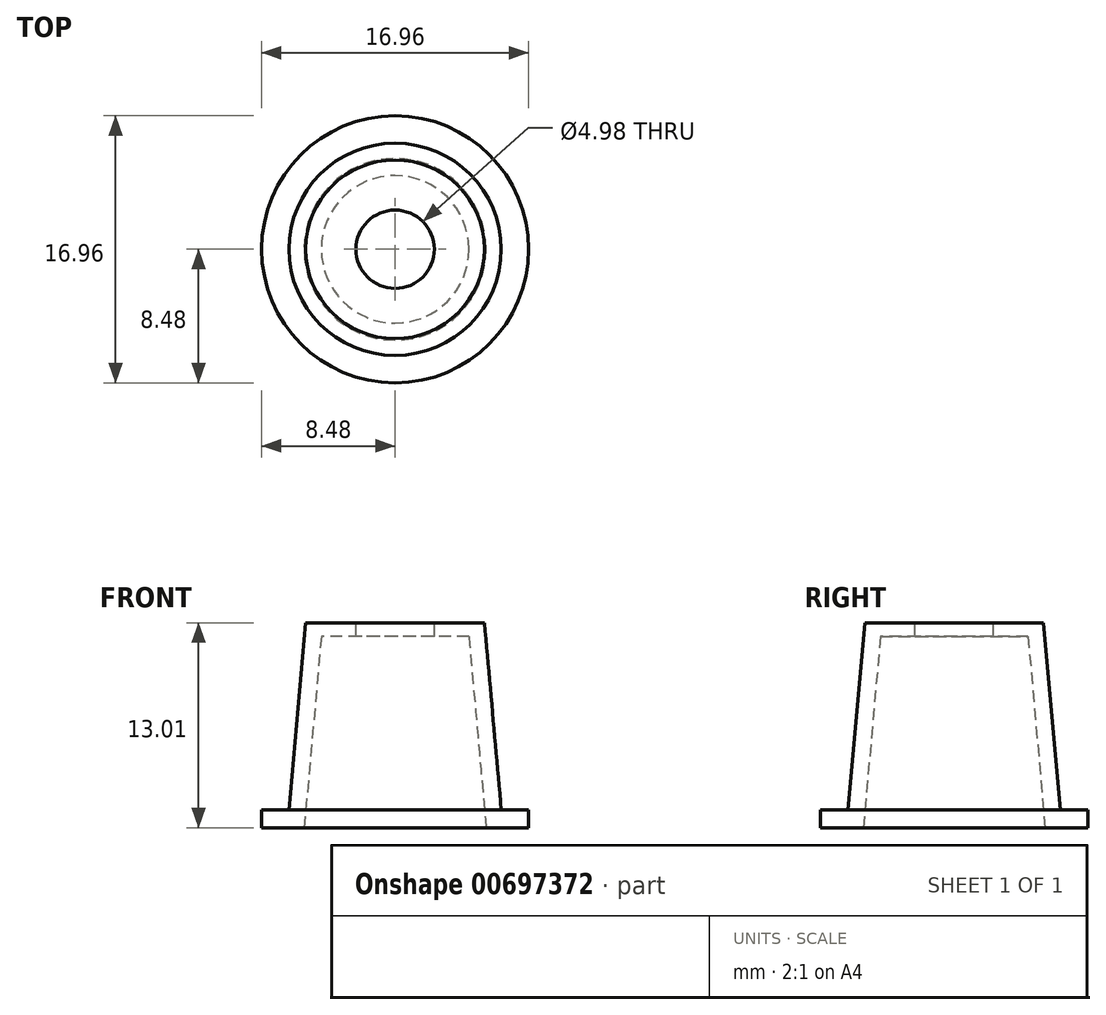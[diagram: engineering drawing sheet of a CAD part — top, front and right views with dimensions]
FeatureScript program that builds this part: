
annotation { "Feature Type Name" : "Feature", "Feature Type Description" : "" }
export const myFeature = defineFeature(function(context is Context, id is Id, definition is map)
    precondition{}
    {
        {
            var Q0;
            Q0=qCreatedBy(makeId("Front.planeOp"),FACE);
            var sketch = newSketch(context, id + "F0", { "sketchPlane" : qUnion([Q0])});
            skLineSegment(sketch, "E0", {"start": v(-8.48, 0) * mm, "end": v(-8.48, 1.13) * mm});
            skLineSegment(sketch, "E1", {"start": v(-8.48, 1.13) * mm, "end": v(-6.74, 1.13) * mm});
            skLineSegment(sketch, "E2", {"start": v(-5.68, 13.01) * mm, "end": v(-6.74, 1.13) * mm});
            skLineSegment(sketch, "E3", {"start": v(-5.68, 13.01) * mm, "end": v(-2.49, 13.01) * mm});
            skLineSegment(sketch, "E4", {"start": v(-2.49, 13.01) * mm, "end": v(-2.49, 12.16) * mm});
            skLineSegment(sketch, "E5", {"start": v(-2.49, 12.16) * mm, "end": v(-4.69, 12.16) * mm});
            skLineSegment(sketch, "E6", {"start": v(-4.69, 12.16) * mm, "end": v(-5.77, 0) * mm});
            skLineSegment(sketch, "E7", {"start": v(-8.48, 0) * mm, "end": v(-5.77, 0) * mm});
            skLineSegment(sketch, "E8", {"start": v(0, 15.54) * mm, "end": v(0, -0.82) * mm, "construction": true});
            skSolve(sketch);
        }
        {
            var Q0;
            Q0=makeQuery(id+"F0.imprint","IMPRINT",FACE,{"disambiguationData":[TD([[makeQuery(id+"F0.imprint","IMPRINT",EDGE,{"derivedFrom":sQuery(id+"F0.wireOp",EDGE,"E0")}),-1.0]])]});
            var Q1;
            Q1=sQuery(id+"F0.wireOp",EDGE,"E8");
            revolve(context, id + "F1", {"surfaceOperationType" : NewSurfaceOperationType.NEW, "entities" : qUnion([Q0]), "axis" : qUnion([Q1]), "revolveType" : RevolveType.FULL});
        }
    });
